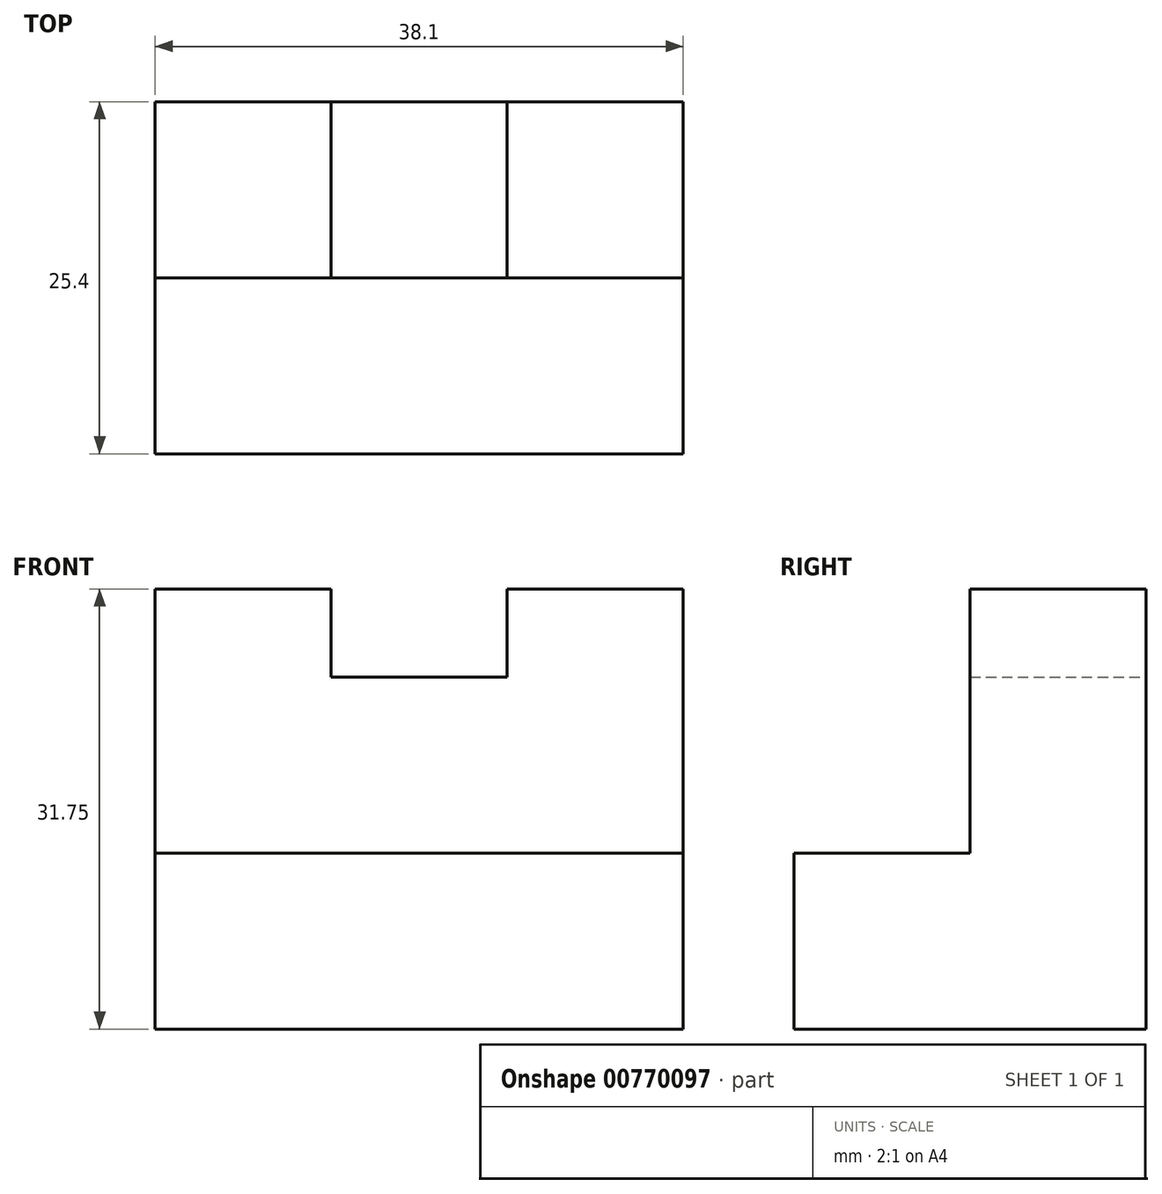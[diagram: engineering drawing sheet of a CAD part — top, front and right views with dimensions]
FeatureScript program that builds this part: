
annotation { "Feature Type Name" : "Feature", "Feature Type Description" : "" }
export const myFeature = defineFeature(function(context is Context, id is Id, definition is map)
    precondition{}
    {
        {
            var Q0;
            Q0=qCreatedBy(makeId("Front.planeOp"),FACE);
            var sketch = newSketch(context, id + "F0", { "sketchPlane" : qUnion([Q0])});
            skLineSegment(sketch, "E0", {"start": v(0, 0) * mm, "end": v(38.1, 0) * mm});
            skLineSegment(sketch, "E1", {"start": v(38.1, 0) * mm, "end": v(38.1, 31.75) * mm});
            skLineSegment(sketch, "E2", {"start": v(38.1, 31.75) * mm, "end": v(0, 31.75) * mm});
            skLineSegment(sketch, "E3", {"start": v(0, 31.75) * mm, "end": v(0, 0) * mm});
            skSolve(sketch);
        }
        {
            var Q0;
            Q0 = qSketchRegion(id + "F0", true);
            extrude(context, id + "F1", {"entities" : qUnion([Q0]), "depth" : 25.4 * mm, "offsetDistance" : 25.4 * mm});
        }
        {
            var Q0;
            Q0=makeQuery(id+"F1.opExtrude","SWEPT_FACE",FACE,{"disambiguationData":[OSD([sQuery(id+"F0.wireOp",EDGE,"E1")])]});
            var sketch = newSketch(context, id + "F2", { "sketchPlane" : qUnion([Q0])});
            skLineSegment(sketch, "E4", {"start": v(-25.4, 0) * mm, "end": v(-25.4, 12.7) * mm});
            skLineSegment(sketch, "E5", {"start": v(-25.4, 12.7) * mm, "end": v(-12.7, 12.7) * mm});
            skLineSegment(sketch, "E6", {"start": v(-12.7, 12.7) * mm, "end": v(-12.7, 31.75) * mm});
            skSolve(sketch);
        }
        {
            var Q0;
            Q0 = qSketchRegion(id + "F2", true);
            var Q1;
            {var subQ0=sQuery(id+"F2.wireOp",EDGE,"E5");Q1=makeQuery(id+"F2.imprint","IMPRINT",FACE,{"disambiguationData":[TD([[makeQuery(id+"F2.imprint","IMPRINT",EDGE,{"derivedFrom":subQ0}),1.0]])]});}
            extrude(context, id + "F3", {"entities" : qUnion([Q0, Q1]), "operationType" : NewBodyOperationType.REMOVE, "oppositeDirection" : true, "depth" : 38.1 * mm, "offsetDistance" : 25.4 * mm});
        }
        {
            var Q0;
            Q0=makeQuery(id+"F1.opExtrude","SWEPT_FACE",FACE,{"disambiguationData":[OSD([sQuery(id+"F0.wireOp",EDGE,"E2")])]});
            var sketch = newSketch(context, id + "F4", { "sketchPlane" : qUnion([Q0])});
            skLineSegment(sketch, "E7", {"start": v(12.7, -12.7) * mm, "end": v(12.7, 0) * mm});
            skLineSegment(sketch, "E8", {"start": v(12.7, 0) * mm, "end": v(25.4, 0) * mm});
            skLineSegment(sketch, "E9", {"start": v(25.4, 0) * mm, "end": v(25.4, -12.7) * mm});
            skSolve(sketch);
        }
        {
            var Q0;
            {var subQ0=sQuery(id+"F4.wireOp",EDGE,"E7");Q0=makeQuery(id+"F4.imprint","IMPRINT",FACE,{"disambiguationData":[TD([[makeQuery(id+"F4.imprint","IMPRINT",EDGE,{"derivedFrom":subQ0}),-1.0]])]});}
            extrude(context, id + "F5", {"entities" : qUnion([Q0]), "operationType" : NewBodyOperationType.REMOVE, "oppositeDirection" : true, "depth" : 6.35 * mm, "offsetDistance" : 25.4 * mm});
        }
    });
